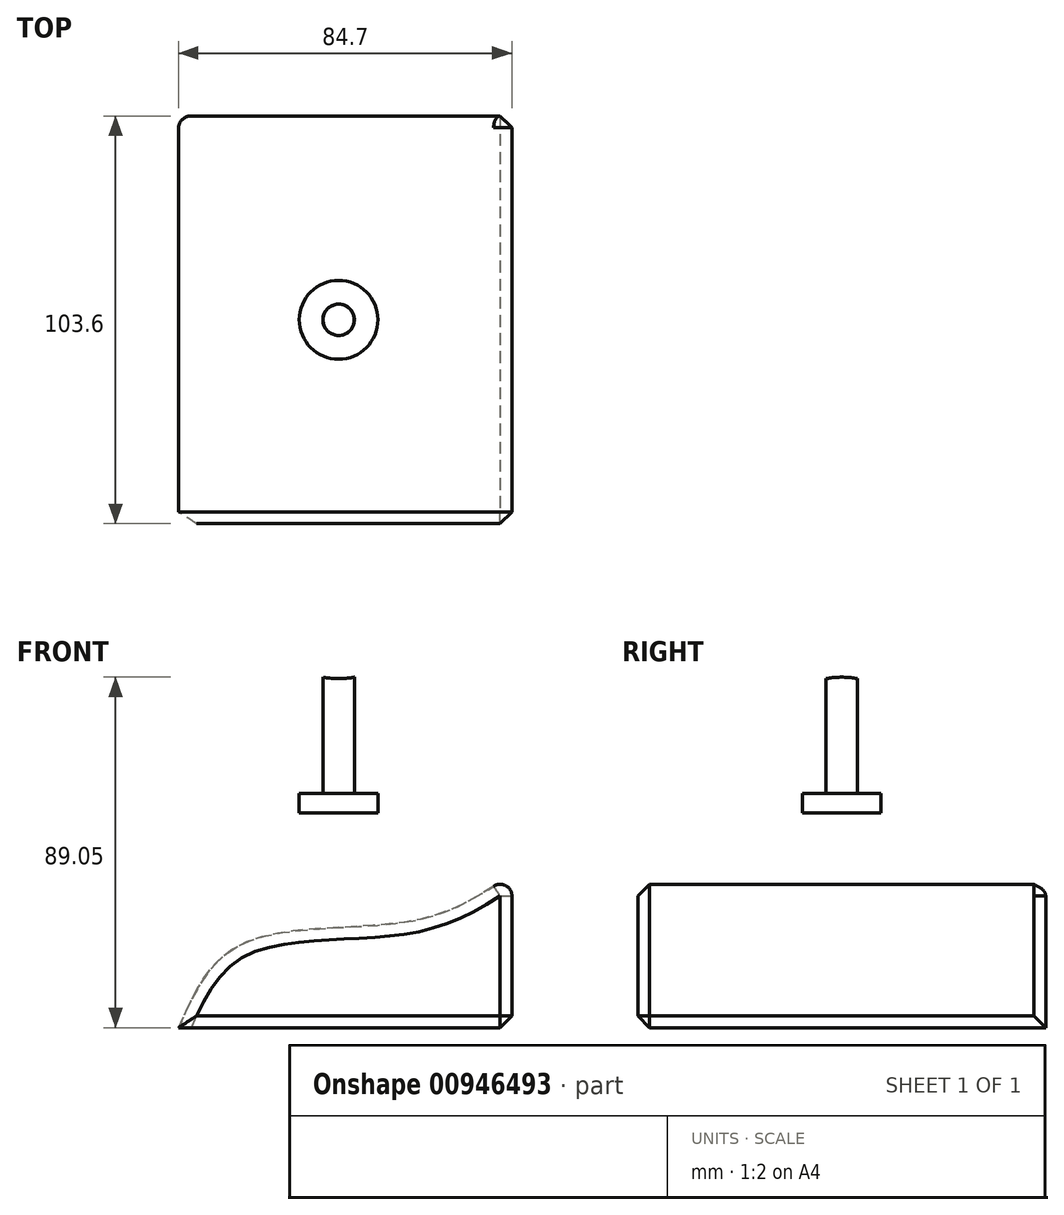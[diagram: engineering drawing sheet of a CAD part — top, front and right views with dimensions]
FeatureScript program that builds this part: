
annotation { "Feature Type Name" : "Feature", "Feature Type Description" : "" }
export const myFeature = defineFeature(function(context is Context, id is Id, definition is map)
    precondition{}
    {
        {
            var Q0;
            Q0=qCreatedBy(makeId("Top.planeOp"),FACE);
            var sketch = newSketch(context, id + "F0", { "sketchPlane" : qUnion([Q0])});
            skCircle(sketch, "E0", {"center": v(-1.4, 0) * mm, "radius": 10 * mm});
            skSolve(sketch);
        }
        {
            var Q0;
            Q0=makeQuery(id+"F0.imprint","IMPRINT",FACE,{"disambiguationData":[TD([[makeQuery(id+"F0.imprint","IMPRINT",EDGE,{"derivedFrom":sQuery(id+"F0.wireOp",EDGE,"E0")}),1.0]])]});
            extrude(context, id + "F1", {"entities" : qUnion([Q0]), "depth" : 5 * mm, "offsetDistance" : 25 * mm});
        }
        {
            var Q0;
            Q0=makeQuery(id+"F1.opExtrude","CAP_FACE",FACE,{"disambiguationData":[OSD([sQuery(id+"F0.wireOp",EDGE,"E0")])],"isStart":false});
            var sketch = newSketch(context, id + "F2", { "sketchPlane" : qUnion([Q0])});
            skCircle(sketch, "E1.0", {"center": v(-1.4, 0) * mm, "radius": 10 * mm, "construction": true});
            skCircle(sketch, "E2", {"center": v(-1.4, 0) * mm, "radius": 4 * mm});
            skLineSegment(sketch, "E3", {"start": v(24.27, 13.21) * mm, "end": v(24.27, -6.58) * mm, "construction": true});
            skLineSegment(sketch, "E4", {"start": v(24.27, -6.58) * mm, "end": v(36.74, -5.9) * mm, "construction": true});
            skSolve(sketch);
        }
        {
            var Q0;
            Q0 = qSketchRegion(id + "F2", true);
            extrude(context, id + "F3", {"entities" : qUnion([Q0]), "operationType" : NewBodyOperationType.ADD, "depth" : 50 * mm, "offsetDistance" : 25 * mm});
        }
        {
            var Q0;
            Q0=qCreatedBy(makeId("Front.planeOp"),FACE);
            var sketch = newSketch(context, id + "F4", { "sketchPlane" : qUnion([Q0])});
            skLineSegment(sketch, "E5.0", {"start": v(-5.4, 55) * mm, "end": v(2.6, 55) * mm});
            skCircle(sketch, "E6", {"center": v(-1.4, 55) * mm, "radius": 20.86 * mm});
            skSolve(sketch);
        }
        {
            var Q0;
            Q0 = qSketchRegion(id + "F4", true);
            extrude(context, id + "F5", {"entities" : qUnion([Q0]), "operationType" : NewBodyOperationType.REMOVE, "oppositeDirection" : true, "depth" : 45.2 * mm, "offsetDistance" : 25 * mm, "symmetric" : true});
        }
        {
            var Q0;
            Q0=qCreatedBy(makeId("Front.planeOp"),FACE);
            var sketch = newSketch(context, id + "F6", { "sketchPlane" : qUnion([Q0])});
            skLineSegment(sketch, "E7.bottom", {"start": v(-42.07, -15.44) * mm, "end": v(42.63, -15.44) * mm});
            skLineSegment(sketch, "E7.top", {"start": v(-42.07, -54.53) * mm, "end": v(42.63, -54.53) * mm});
            skLineSegment(sketch, "E7.left", {"start": v(-42.07, -15.44) * mm, "end": v(-42.07, -54.53) * mm});
            skLineSegment(sketch, "E7.right", {"start": v(42.63, -15.44) * mm, "end": v(42.63, -54.53) * mm});
            skSolve(sketch);
        }
        {
            var Q0;
            Q0 = qSketchRegion(id + "F6", true);
            extrude(context, id + "F7", {"entities" : qUnion([Q0]), "depth" : 103.6 * mm, "offsetDistance" : 25 * mm, "symmetric" : true});
        }
        {
            var Q0;
            Q0=makeQuery(id+"F7.opExtrude","CAP_FACE",FACE,{"disambiguationData":[OSD([sQuery(id+"F6.wireOp",EDGE,"E7.bottom"),sQuery(id+"F6.wireOp",EDGE,"E7.top"),sQuery(id+"F6.wireOp",EDGE,"E7.left"),sQuery(id+"F6.wireOp",EDGE,"E7.right")])],"isStart":false});
            var sketch = newSketch(context, id + "F8", { "sketchPlane" : qUnion([Q0])});
            skFitSpline(sketch, "E8", {"points": [v(-42.07, -54.53) * mm, v(-25.92, -33.28) * mm, v(17.7, -27.34) * mm, v(42.63, -15.44) * mm], "startDerivative": vector(37.27, 84.72) * mm, "endDerivative": vector(69.45, 47.9) * mm});
            skLineSegment(sketch, "E9", {"start": v(-42.07, -54.53) * mm, "end": v(-42.07, -15.44) * mm});
            skLineSegment(sketch, "E10", {"start": v(-42.07, -15.44) * mm, "end": v(42.63, -15.44) * mm});
            skSolve(sketch);
        }
        {
            var Q0;
            Q0 = qSketchRegion(id + "F8", true);
            extrude(context, id + "F9", {"entities" : qUnion([Q0]), "operationType" : NewBodyOperationType.REMOVE, "oppositeDirection" : true, "depth" : 126.7 * mm, "offsetDistance" : 25 * mm});
        }
        {
            var Q0;
            Q0=makeQuery(id+"F9.boolean.opBoolean","COPY",EDGE,{"derivedFrom":makeQuery(id+"F9.opExtrude","CAP_EDGE",EDGE,{"disambiguationData":[OSD([sQuery(id+"F8.wireOp",EDGE,"E8")])],"isStart":true})});
            var Q1;
            Q1=makeQuery(id+"F9.boolean.opBoolean","INTERSECT",EDGE,{"derivedFrom":[makeQuery(id+"F7.opExtrude","CAP_FACE",FACE,{"disambiguationData":[OSD([sQuery(id+"F6.wireOp",EDGE,"E7.bottom"),sQuery(id+"F6.wireOp",EDGE,"E7.top"),sQuery(id+"F6.wireOp",EDGE,"E7.left"),sQuery(id+"F6.wireOp",EDGE,"E7.right")])],"isStart":true}),makeQuery(id+"F9.opExtrude","SWEPT_FACE",FACE,{"disambiguationData":[OSD([sQuery(id+"F8.wireOp",EDGE,"E8")])]})]});
            var Q2;
            {var subQ0=sQuery(id+"F6.wireOp",EDGE,"E7.right");Q2=makeQuery(id+"F9.boolean.opBoolean","MERGE",EDGE,{"derivedFrom":[makeQuery(id+"F7.opExtrude","SWEPT_EDGE",EDGE,{"disambiguationData":[OSD([sQuery(id+"F6.wireOp",EDGE,"E7.bottom"),subQ0])]})],"fromTools":[makeQuery(id+"F9.opExtrude","SWEPT_EDGE",EDGE,{"disambiguationData":[OSD([subQ0,sQuery(id+"F8.wireOp",EDGE,"E8"),sQuery(id+"F8.wireOp",EDGE,"E10")])]})]});}
            fillet(context, id + "F10", {"entities" : qUnion([Q0, Q1, Q2]), "radius" : 3 * mm, "tangentPropagation" : true, "allowEdgeOverflow" : false});
        }
        {
            var Q0;
            Q0=makeQuery(id+"F7.opExtrude","CAP_EDGE",EDGE,{"disambiguationData":[OSD([sQuery(id+"F6.wireOp",EDGE,"E7.top")])],"isStart":false});
            var Q1;
            Q1=makeQuery(id+"F7.opExtrude","CAP_EDGE",EDGE,{"disambiguationData":[OSD([sQuery(id+"F6.wireOp",EDGE,"E7.right")])],"isStart":false});
            var Q2;
            Q2=makeQuery(id+"F7.opExtrude","SWEPT_EDGE",EDGE,{"disambiguationData":[OSD([sQuery(id+"F6.wireOp",EDGE,"E7.top"),sQuery(id+"F6.wireOp",EDGE,"E7.right")])]});
            var Q3;
            Q3=makeQuery(id+"F7.opExtrude","CAP_EDGE",EDGE,{"disambiguationData":[OSD([sQuery(id+"F6.wireOp",EDGE,"E7.right")])],"isStart":true});
            chamfer(context, id + "F11", {"entities" : qUnion([Q0, Q1, Q2, Q3]), "width" : 3 * mm, "tangentPropagation" : true});
        }
    });
